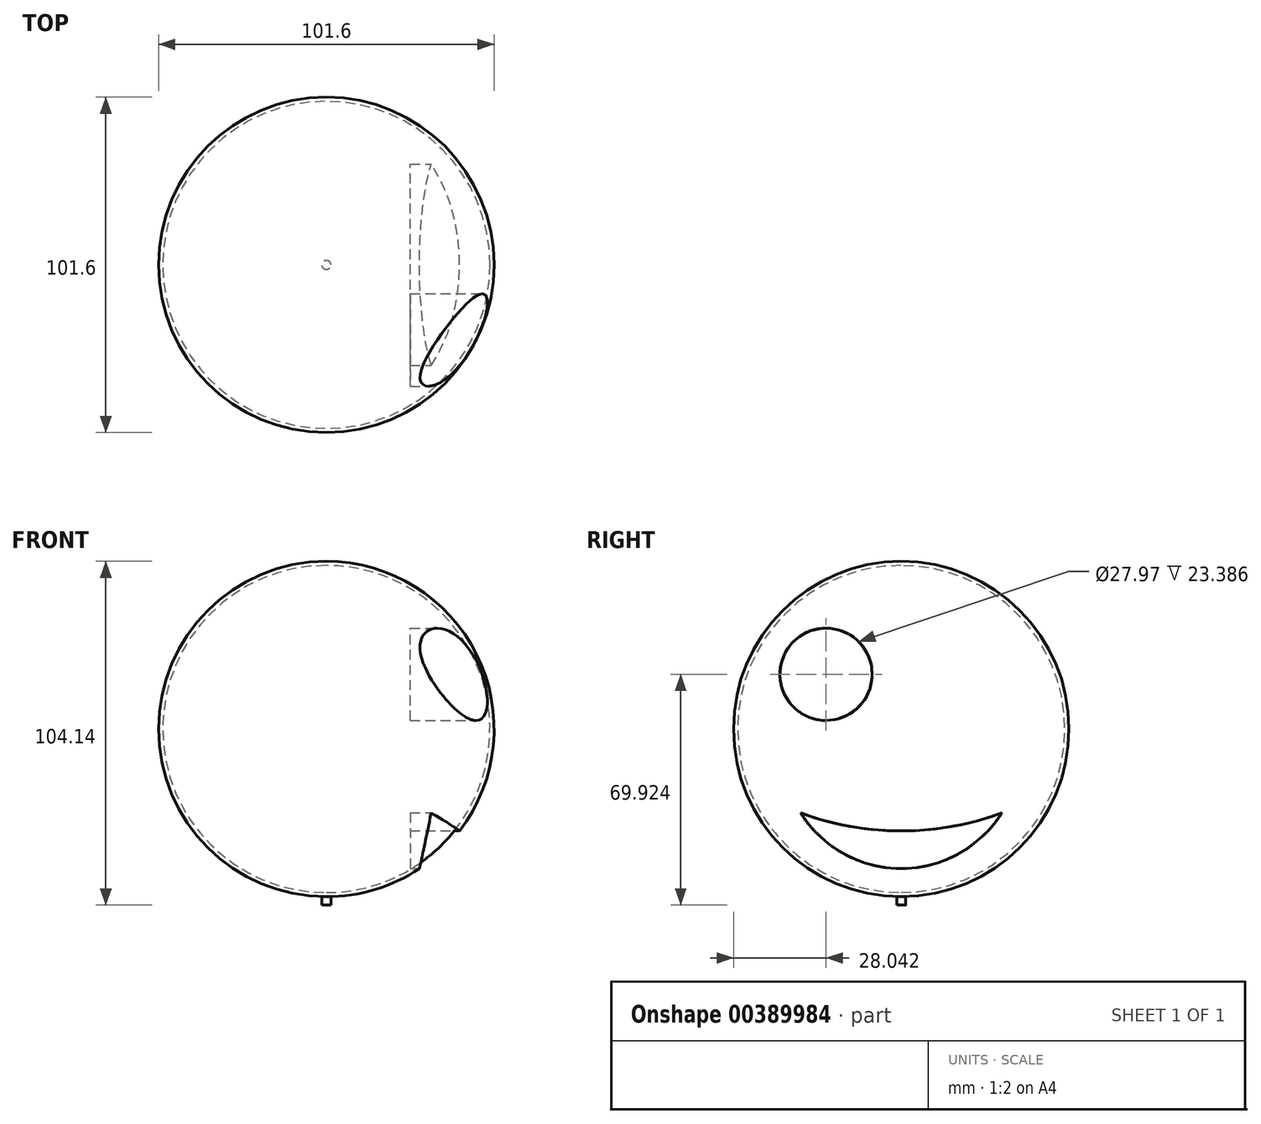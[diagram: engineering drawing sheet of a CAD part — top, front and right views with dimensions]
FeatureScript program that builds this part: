
annotation { "Feature Type Name" : "Feature", "Feature Type Description" : "" }
export const myFeature = defineFeature(function(context is Context, id is Id, definition is map)
    precondition{}
    {
        {
            var Q0;
            Q0=qCreatedBy(makeId("Front.planeOp"),FACE);
            var sketch = newSketch(context, id + "F0", { "sketchPlane" : qUnion([Q0])});
            skCircle(sketch, "E0", {"center": v(0, 0) * mm, "radius": 50.8 * mm});
            skLineSegment(sketch, "E1", {"start": v(0, 50.8) * mm, "end": v(0, -50.8) * mm, "construction": true});
            skLineSegment(sketch, "E2", {"start": v(0, 50.8) * mm, "end": v(0, -50.8) * mm});
            skSolve(sketch);
        }
        {
            var Q0;
            {var subQ0=sQuery(id+"F0.wireOp",EDGE,"E2");Q0=makeQuery(id+"F0.imprint","IMPRINT",FACE,{"disambiguationData":[TD([[makeQuery(id+"F0.imprint","IMPRINT",EDGE,{"derivedFrom":subQ0}),-1.0]])]});}
            var Q1;
            Q1=sQuery(id+"F0.wireOp",EDGE,"E2");
            revolve(context, id + "F1", {"entities" : qUnion([Q0]), "axis" : qUnion([Q1]), "revolveType" : RevolveType.FULL});
        }
        {
            var Q0;
            Q0=qCreatedBy(makeId("Right.planeOp"),FACE);
            cPlane(context, id + "F2", {"entities" : qUnion([Q0]), "cplaneType" : CPlaneType.OFFSET, "offset" : 50.8 * mm, "width" : 152.4 * mm, "height" : 152.4 * mm});
        }
        {
            var Q0;
            Q0=qCreatedBy(id+"F2.planeOp",FACE);
            var sketch = newSketch(context, id + "F3", { "sketchPlane" : qUnion([Q0])});
            skCircle(sketch, "E3", {"center": v(-22.76, 16.58) * mm, "radius": 13.98 * mm});
            skCircle(sketch, "E4.MirrorC", {"center": v(22.76, 16.58) * mm, "radius": 13.98 * mm});
            skArc(sketch, "E5", {"start": v(-30.48, -25.4) * mm, "mid": v(0, -42.26) * mm, "end": v(30.48, -25.4) * mm});
            skArc(sketch, "E6", {"start": v(-30.48, -25.4) * mm, "mid": v(0, -30.86) * mm, "end": v(30.48, -25.4) * mm});
            skSolve(sketch);
        }
        {
            var Q0;
            Q0=makeQuery(id+"F3.imprint","IMPRINT",FACE,{"disambiguationData":[TD([[makeQuery(id+"F3.imprint","IMPRINT",EDGE,{"derivedFrom":sQuery(id+"F3.wireOp",EDGE,"E3")}),1.0]])]});
            var Q1;
            Q1=makeQuery(id+"F3.imprint","IMPRINT",FACE,{"disambiguationData":[TD([[makeQuery(id+"F3.imprint","IMPRINT",EDGE,{"derivedFrom":sQuery(id+"F3.wireOp",EDGE,"E5")}),1.0]])]});
            var Q2;
            Q2=makeQuery(id+"F3.imprint","IMPRINT",FACE,{"disambiguationData":[TD([[makeQuery(id+"F3.imprint","IMPRINT",EDGE,{"derivedFrom":sQuery(id+"F3.wireOp",EDGE,"E4.MirrorC")}),-1.0]])]});
            extrude(context, id + "F4", {"entities" : qUnion([Q0, Q1, Q2]), "operationType" : NewBodyOperationType.REMOVE, "oppositeDirection" : true, "depth" : 25.4 * mm});
        }
        {
            var Q0;
            Q0=qCreatedBy(makeId("Right.planeOp"),FACE);
            var sketch = newSketch(context, id + "F5", { "sketchPlane" : qUnion([Q0])});
            skCircle(sketch, "E7", {"center": v(0, 0) * mm, "radius": 49.53 * mm});
            skLineSegment(sketch, "E8", {"start": v(0, 49.53) * mm, "end": v(0, -49.53) * mm});
            skSolve(sketch);
        }
        {
            var Q0;
            {var subQ0=sQuery(id+"F5.wireOp",EDGE,"E8");Q0=makeQuery(id+"F5.imprint","IMPRINT",FACE,{"disambiguationData":[TD([[makeQuery(id+"F5.imprint","IMPRINT",EDGE,{"derivedFrom":subQ0}),-1.0]])]});}
            var Q1;
            Q1=sQuery(id+"F5.wireOp",EDGE,"E8");
            revolve(context, id + "F6", {"entities" : qUnion([Q0]), "axis" : qUnion([Q1]), "revolveType" : RevolveType.FULL});
        }
        {
            var Q0;
            Q0=qCreatedBy(makeId("Front.planeOp"),FACE);
            var sketch = newSketch(context, id + "F7", { "sketchPlane" : qUnion([Q0])});
            skArc(sketch, "E9", {"start": v(40.35, -30.86) * mm, "mid": v(-34.74, 37.06) * mm, "end": v(28.2, -42.26) * mm});
            skPoint(sketch, "E10", {"position": v(0, -50.8) * mm});
            skSolve(sketch);
        }
        {
            var Q0;
            Q0=qCreatedBy(makeId("Top.planeOp"),FACE);
            var Q1;
            Q1=sQuery(id+"F7.wireOp",VERTEX,"E10");
            cPlane(context, id + "F8", {"entities" : qUnion([Q0, Q1]), "cplaneType" : CPlaneType.PLANE_POINT, "offset" : 25.4 * mm, "width" : 152.4 * mm, "height" : 152.4 * mm});
        }
        {
            var Q0;
            Q0=qCreatedBy(id+"F8.planeOp",FACE);
            var sketch = newSketch(context, id + "F9", { "sketchPlane" : qUnion([Q0])});
            skCircle(sketch, "E11", {"center": v(0, 0) * mm, "radius": 1.37 * mm});
            skSolve(sketch);
        }
        {
            var Q0;
            Q0=makeQuery(id+"F9.imprint","IMPRINT",FACE,{"disambiguationData":[TD([[makeQuery(id+"F9.imprint","IMPRINT",EDGE,{"derivedFrom":sQuery(id+"F9.wireOp",EDGE,"E11")}),1.0]])]});
            extrude(context, id + "F10", {"entities" : qUnion([Q0]), "oppositeDirection" : true, "depth" : 2.54 * mm});
        }
    });
